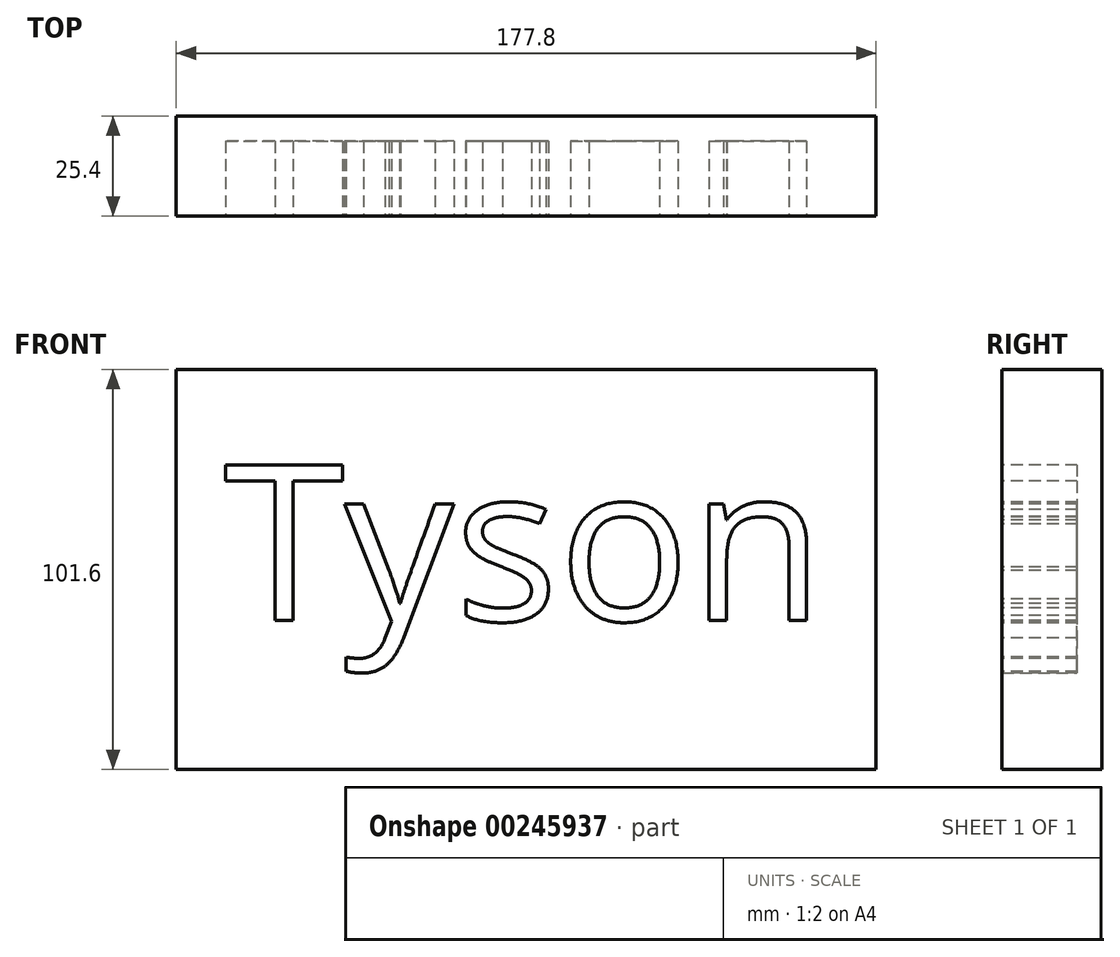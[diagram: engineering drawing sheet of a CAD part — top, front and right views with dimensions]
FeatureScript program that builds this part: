
annotation { "Feature Type Name" : "Feature", "Feature Type Description" : "" }
export const myFeature = defineFeature(function(context is Context, id is Id, definition is map)
    precondition{}
    {
        {
            var Q0;
            Q0=qCreatedBy(makeId("Front.planeOp"),FACE);
            var sketch = newSketch(context, id + "F0", { "sketchPlane" : qUnion([Q0])});
            skLineSegment(sketch, "E0", {"start": v(-118.48, 48) * mm, "end": v(-118.48, -53.6) * mm});
            skLineSegment(sketch, "E1", {"start": v(-118.48, -53.6) * mm, "end": v(59.32, -53.6) * mm});
            skLineSegment(sketch, "E2", {"start": v(59.32, -53.6) * mm, "end": v(59.32, 48) * mm});
            skLineSegment(sketch, "E3", {"start": v(59.32, 48) * mm, "end": v(-118.48, 48) * mm});
            skSolve(sketch);
        }
        {
            var Q0;
            Q0 = qSketchRegion(id + "F0", true);
            extrude(context, id + "F1", {"entities" : qUnion([Q0]), "depth" : 25.4 * mm});
        }
        {
            var Q0;
            Q0=makeQuery(id+"F1.opExtrude","CAP_FACE",FACE,{"disambiguationData":[OSD([sQuery(id+"F0.wireOp",EDGE,"E0"),sQuery(id+"F0.wireOp",EDGE,"E1"),sQuery(id+"F0.wireOp",EDGE,"E2"),sQuery(id+"F0.wireOp",EDGE,"E3")])],"isStart":false});
            var sketch = newSketch(context, id + "F2", { "sketchPlane" : qUnion([Q0])});
            skSolve(sketch);
        }
        {
            var Q0;
            Q0=makeQuery(id+"F2.imprint","IMPRINT",FACE,{"disambiguationData":[TD([[makeQuery(id+"F2.imprint","IMPRINT",EDGE,{"derivedFrom":makeQuery(id+"F1.opExtrude","CAP_EDGE",EDGE,{"disambiguationData":[OSD([sQuery(id+"F0.wireOp",EDGE,"E0")])],"isStart":false})}),1.0]])]});
            var sketch = newSketch(context, id + "F3", { "sketchPlane" : qUnion([Q0])});
            skText(sketch, "E4", { "text": "Tyson", "fontName": "OpenSans-Regular.ttf"});
            const initialGuessF3  = {"E4": [-0.10641, -0.0158, 1, 0, 0.03991]};
            skSetInitialGuess(sketch, initialGuessF3);
            skSolve(sketch);
        }
        {
            var Q0;
            Q0 = qSketchRegion(id + "F3", true);
            extrude(context, id + "F4", {"entities" : qUnion([Q0]), "operationType" : NewBodyOperationType.REMOVE, "oppositeDirection" : true, "depth" : 19.05 * mm});
        }
    });
